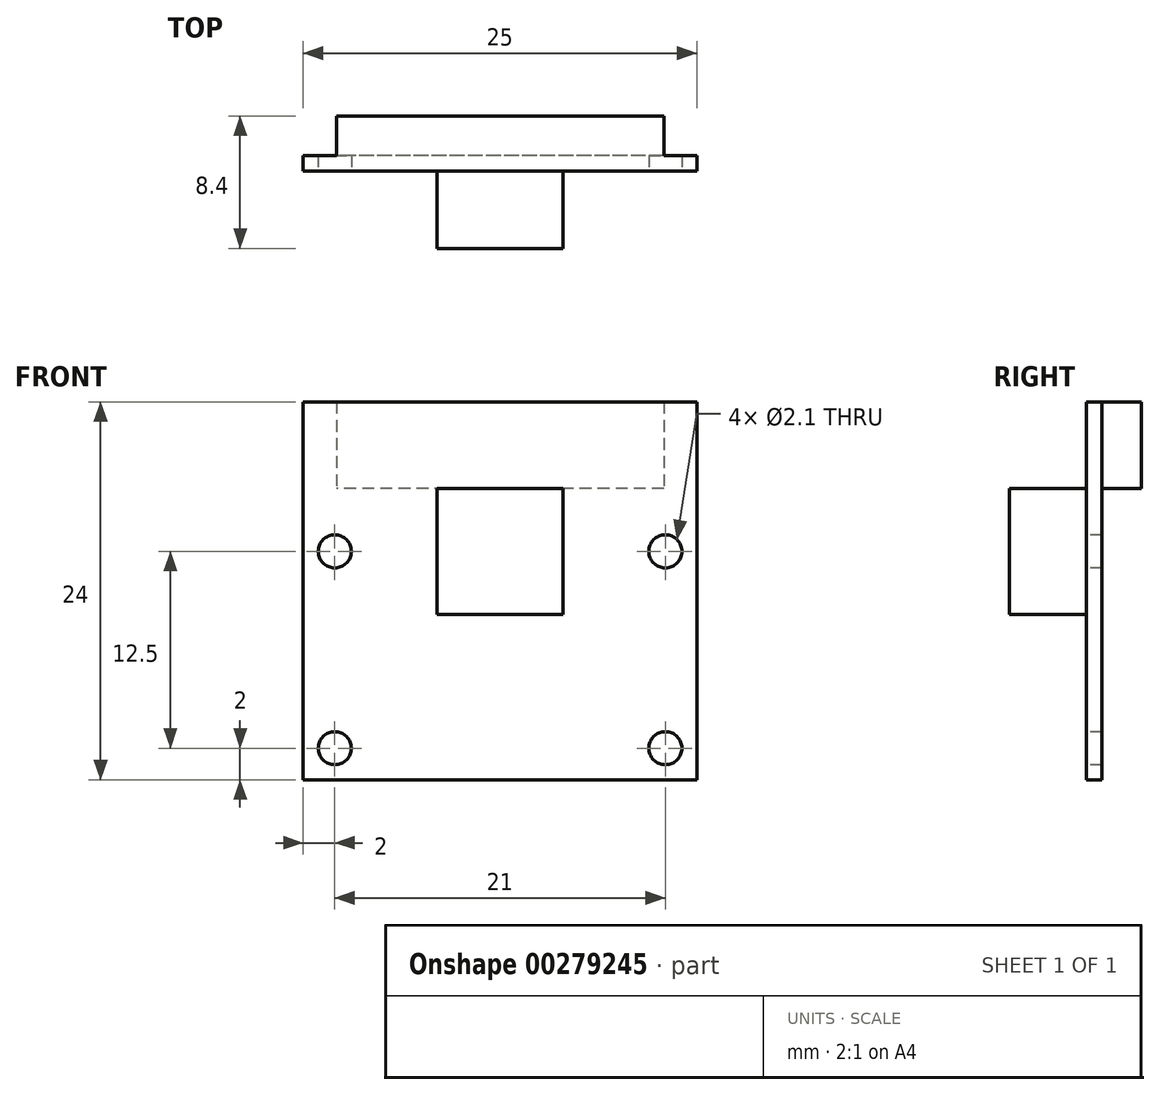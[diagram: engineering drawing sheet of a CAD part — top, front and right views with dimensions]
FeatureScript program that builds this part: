
annotation { "Feature Type Name" : "Feature", "Feature Type Description" : "" }
export const myFeature = defineFeature(function(context is Context, id is Id, definition is map)
    precondition{}
    {
        {
            var Q0;
            Q0=qCreatedBy(makeId("Front.planeOp"),FACE);
            var sketch = newSketch(context, id + "F0", { "sketchPlane" : qUnion([Q0])});
            skLineSegment(sketch, "E0.bottom", {"start": v(12.5, -12) * mm, "end": v(-12.5, -12) * mm});
            skLineSegment(sketch, "E0.top", {"start": v(12.5, 12) * mm, "end": v(-12.5, 12) * mm});
            skLineSegment(sketch, "E0.left", {"start": v(12.5, -12) * mm, "end": v(12.5, 12) * mm});
            skLineSegment(sketch, "E0.right", {"start": v(-12.5, -12) * mm, "end": v(-12.5, 12) * mm});
            skPoint(sketch, "E0.middle", {"position": v(0, 0) * mm});
            skSolve(sketch);
        }
        {
            var Q0;
            Q0=makeQuery(id+"F0.imprint","IMPRINT",FACE,{"disambiguationData":[TD([[makeQuery(id+"F0.imprint","IMPRINT",EDGE,{"derivedFrom":sQuery(id+"F0.wireOp",EDGE,"E0.bottom")}),-1.0]])]});
            extrude(context, id + "F1", {"entities" : qUnion([Q0]), "endBound" : BoundingType.SYMMETRIC, "depth" : 1 * mm});
        }
        {
            var Q0;
            Q0=makeQuery(id+"F1.opExtrude","CAP_FACE",FACE,{"disambiguationData":[OSD([sQuery(id+"F0.wireOp",EDGE,"E0.bottom"),sQuery(id+"F0.wireOp",EDGE,"E0.top"),sQuery(id+"F0.wireOp",EDGE,"E0.left"),sQuery(id+"F0.wireOp",EDGE,"E0.right")])],"isStart":false});
            var sketch = newSketch(context, id + "F2", { "sketchPlane" : qUnion([Q0])});
            skCircle(sketch, "E1", {"center": v(-10.5, -10) * mm, "radius": 1 * mm});
            skCircle(sketch, "E2", {"center": v(-10.5, 2.5) * mm, "radius": 1 * mm});
            skCircle(sketch, "E3.MirrorC", {"center": v(10.5, 2.5) * mm, "radius": 1 * mm});
            skCircle(sketch, "E4.MirrorC", {"center": v(10.5, -10) * mm, "radius": 1 * mm});
            skSolve(sketch);
        }
        {
            var Q0;
            Q0=sQuery(id+"F2.wireOp",VERTEX,"E2.center");
            var Q1;
            Q1=sQuery(id+"F2.wireOp",VERTEX,"E1.center");
            var Q2;
            Q2=sQuery(id+"F2.wireOp",VERTEX,"E3.MirrorC.center");
            var Q3;
            Q3=sQuery(id+"F2.wireOp",VERTEX,"E4.MirrorC.center");
            var Q4;
            Q4=makeQuery(id+"F1.opExtrude","SWEPT_BODY",BODY,{"disambiguationData":[OSD([sQuery(id+"F0.wireOp",EDGE,"E0.bottom"),sQuery(id+"F0.wireOp",EDGE,"E0.top"),sQuery(id+"F0.wireOp",EDGE,"E0.left"),sQuery(id+"F0.wireOp",EDGE,"E0.right")])]});
            hole(context, id + "F3", {"style" : HoleStyle.SIMPLE, "endStyle" : HoleEndStyle.THROUGH, "holeDiameter" : 2.1 * mm, "tappedDepth" : 12 * mm, "tapClearance" : 3, "locations" : qUnion([Q0, Q1, Q2, Q3]), "scope" : qUnion([Q4])});
        }
        {
            var Q0;
            Q0=makeQuery(id+"F1.opExtrude","CAP_FACE",FACE,{"disambiguationData":[OSD([sQuery(id+"F0.wireOp",EDGE,"E0.bottom"),sQuery(id+"F0.wireOp",EDGE,"E0.top"),sQuery(id+"F0.wireOp",EDGE,"E0.left"),sQuery(id+"F0.wireOp",EDGE,"E0.right")])],"isStart":true});
            var sketch = newSketch(context, id + "F4", { "sketchPlane" : qUnion([Q0])});
            skLineSegment(sketch, "E5.bottom", {"start": v(-10.4, 12) * mm, "end": v(10.4, 12) * mm});
            skLineSegment(sketch, "E5.top", {"start": v(-10.4, 6.5) * mm, "end": v(10.4, 6.5) * mm});
            skLineSegment(sketch, "E5.left", {"start": v(-10.4, 12) * mm, "end": v(-10.4, 6.5) * mm});
            skLineSegment(sketch, "E5.right", {"start": v(10.4, 12) * mm, "end": v(10.4, 6.5) * mm});
            skSolve(sketch);
        }
        {
            var Q0;
            Q0=makeQuery(id+"F4.imprint","IMPRINT",FACE,{"disambiguationData":[TD([[makeQuery(id+"F4.imprint","IMPRINT",EDGE,{"derivedFrom":sQuery(id+"F4.wireOp",EDGE,"E5.bottom")}),-1.0]])]});
            extrude(context, id + "F5", {"entities" : qUnion([Q0]), "operationType" : NewBodyOperationType.ADD, "depth" : 2.5 * mm});
        }
        {
            var Q0;
            Q0=makeQuery(id+"F1.opExtrude","CAP_FACE",FACE,{"disambiguationData":[OSD([sQuery(id+"F0.wireOp",EDGE,"E0.bottom"),sQuery(id+"F0.wireOp",EDGE,"E0.top"),sQuery(id+"F0.wireOp",EDGE,"E0.left"),sQuery(id+"F0.wireOp",EDGE,"E0.right")])],"isStart":false});
            var sketch = newSketch(context, id + "F6", { "sketchPlane" : qUnion([Q0])});
            skLineSegment(sketch, "E6.bottom", {"start": v(4, -1.5) * mm, "end": v(-4, -1.5) * mm});
            skLineSegment(sketch, "E6.top", {"start": v(4, 6.5) * mm, "end": v(-4, 6.5) * mm});
            skLineSegment(sketch, "E6.left", {"start": v(4, -1.5) * mm, "end": v(4, 6.5) * mm});
            skLineSegment(sketch, "E6.right", {"start": v(-4, -1.5) * mm, "end": v(-4, 6.5) * mm});
            skPoint(sketch, "E6.middle", {"position": v(0, 2.5) * mm});
            skSolve(sketch);
        }
        {
            var Q0;
            Q0=makeQuery(id+"F6.imprint","IMPRINT",FACE,{"disambiguationData":[TD([[makeQuery(id+"F6.imprint","IMPRINT",EDGE,{"derivedFrom":sQuery(id+"F6.wireOp",EDGE,"E6.bottom")}),-1.0]])]});
            extrude(context, id + "F7", {"entities" : qUnion([Q0]), "operationType" : NewBodyOperationType.ADD, "depth" : 4.9 * mm});
        }
    });
